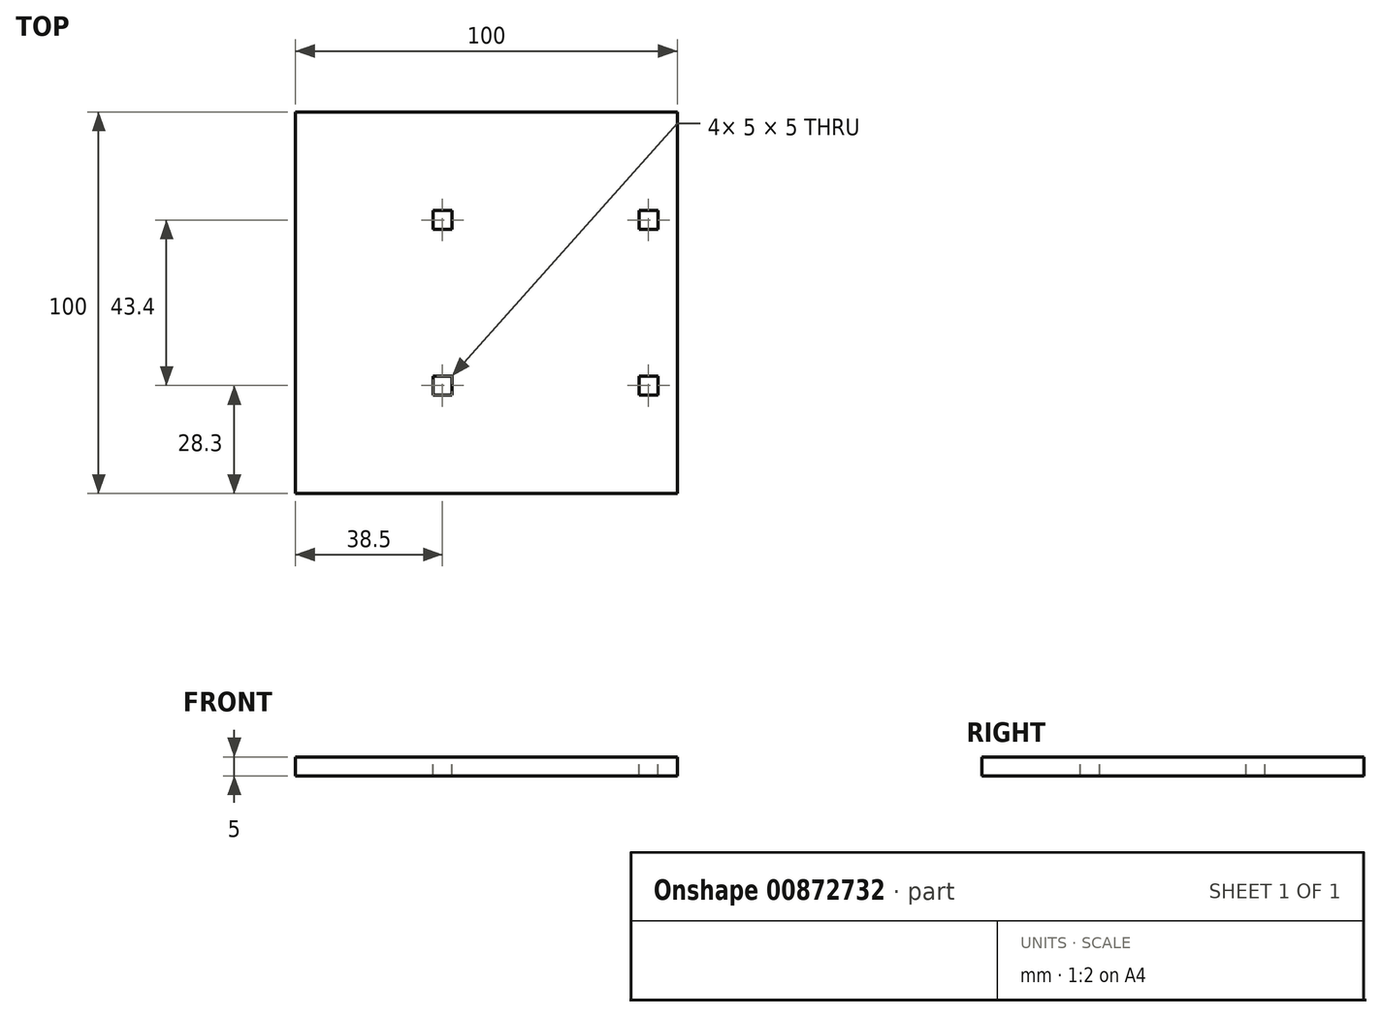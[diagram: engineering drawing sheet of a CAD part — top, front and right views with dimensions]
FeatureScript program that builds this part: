
annotation { "Feature Type Name" : "Feature", "Feature Type Description" : "" }
export const myFeature = defineFeature(function(context is Context, id is Id, definition is map)
    precondition{}
    {
        {
            var Q0;
            Q0=qCreatedBy(makeId("Top.planeOp"),FACE);
            var sketch = newSketch(context, id + "F0", { "sketchPlane" : qUnion([Q0])});
            skLineSegment(sketch, "E0.bottom", {"start": v(-50, 50) * mm, "end": v(50, 50) * mm});
            skLineSegment(sketch, "E0.top", {"start": v(-50, -50) * mm, "end": v(50, -50) * mm});
            skLineSegment(sketch, "E0.left", {"start": v(-50, 50) * mm, "end": v(-50, -50) * mm});
            skLineSegment(sketch, "E0.right", {"start": v(50, 50) * mm, "end": v(50, -50) * mm});
            skSolve(sketch);
        }
        {
            var Q0;
            Q0=makeQuery(id+"F0.imprint","IMPRINT",FACE,{"disambiguationData":[TD([[makeQuery(id+"F0.imprint","IMPRINT",EDGE,{"derivedFrom":sQuery(id+"F0.wireOp",EDGE,"E0.bottom")}),-1.0]])]});
            extrude(context, id + "F1", {"entities" : qUnion([Q0]), "depth" : 5 * mm, "offsetDistance" : 25 * mm});
        }
        {
            var Q0;
            Q0=makeQuery(id+"F1.opExtrude","CAP_FACE",FACE,{"disambiguationData":[OSD([sQuery(id+"F0.wireOp",EDGE,"E0.bottom"),sQuery(id+"F0.wireOp",EDGE,"E0.top"),sQuery(id+"F0.wireOp",EDGE,"E0.left"),sQuery(id+"F0.wireOp",EDGE,"E0.right")])],"isStart":false});
            var sketch = newSketch(context, id + "F2", { "sketchPlane" : qUnion([Q0])});
            skLineSegment(sketch, "E1.bottom", {"start": v(-14, 24.2) * mm, "end": v(-9, 24.2) * mm});
            skLineSegment(sketch, "E1.top", {"start": v(-14, 19.2) * mm, "end": v(-9, 19.2) * mm});
            skLineSegment(sketch, "E1.left", {"start": v(-14, 24.2) * mm, "end": v(-14, 19.2) * mm});
            skLineSegment(sketch, "E1.right", {"start": v(-9, 24.2) * mm, "end": v(-9, 19.2) * mm});
            skLineSegment(sketch, "E2.bottom", {"start": v(40, 24.2) * mm, "end": v(45, 24.2) * mm});
            skLineSegment(sketch, "E2.top", {"start": v(40, 19.2) * mm, "end": v(45, 19.2) * mm});
            skLineSegment(sketch, "E2.left", {"start": v(40, 24.2) * mm, "end": v(40, 19.2) * mm});
            skLineSegment(sketch, "E2.right", {"start": v(45, 24.2) * mm, "end": v(45, 19.2) * mm});
            skLineSegment(sketch, "E3.MirrorCS", {"start": v(40, -24.2) * mm, "end": v(40, -19.2) * mm});
            skLineSegment(sketch, "E4.MirrorCS", {"start": v(40, -24.2) * mm, "end": v(45, -24.2) * mm});
            skLineSegment(sketch, "E5.MirrorCS", {"start": v(45, -24.2) * mm, "end": v(45, -19.2) * mm});
            skLineSegment(sketch, "E6.MirrorCS", {"start": v(40, -19.2) * mm, "end": v(45, -19.2) * mm});
            skLineSegment(sketch, "E7.MirrorCS", {"start": v(-14, -24.2) * mm, "end": v(-9, -24.2) * mm});
            skLineSegment(sketch, "E8.MirrorCS", {"start": v(-9, -24.2) * mm, "end": v(-9, -19.2) * mm});
            skLineSegment(sketch, "E9.MirrorCS", {"start": v(-14, -24.2) * mm, "end": v(-14, -19.2) * mm});
            skLineSegment(sketch, "E10.MirrorCS", {"start": v(-14, -19.2) * mm, "end": v(-9, -19.2) * mm});
            skSolve(sketch);
        }
        {
            var Q0;
            Q0=makeQuery(id+"F2.imprint","IMPRINT",FACE,{"disambiguationData":[TD([[makeQuery(id+"F2.imprint","IMPRINT",EDGE,{"derivedFrom":sQuery(id+"F2.wireOp",EDGE,"E1.bottom")}),-1.0]])]});
            var Q1;
            Q1=makeQuery(id+"F2.imprint","IMPRINT",FACE,{"disambiguationData":[TD([[makeQuery(id+"F2.imprint","IMPRINT",EDGE,{"derivedFrom":sQuery(id+"F2.wireOp",EDGE,"E2.bottom")}),-1.0]])]});
            var Q2;
            Q2=makeQuery(id+"F2.imprint","IMPRINT",FACE,{"disambiguationData":[TD([[makeQuery(id+"F2.imprint","IMPRINT",EDGE,{"derivedFrom":sQuery(id+"F2.wireOp",EDGE,"E7.MirrorCS")}),1.0]])]});
            var Q3;
            Q3=makeQuery(id+"F2.imprint","IMPRINT",FACE,{"disambiguationData":[TD([[makeQuery(id+"F2.imprint","IMPRINT",EDGE,{"derivedFrom":sQuery(id+"F2.wireOp",EDGE,"E3.MirrorCS")}),-1.0]])]});
            extrude(context, id + "F3", {"entities" : qUnion([Q0, Q1, Q2, Q3]), "operationType" : NewBodyOperationType.REMOVE, "oppositeDirection" : true, "depth" : 25 * mm, "offsetDistance" : 25 * mm});
        }
    });
